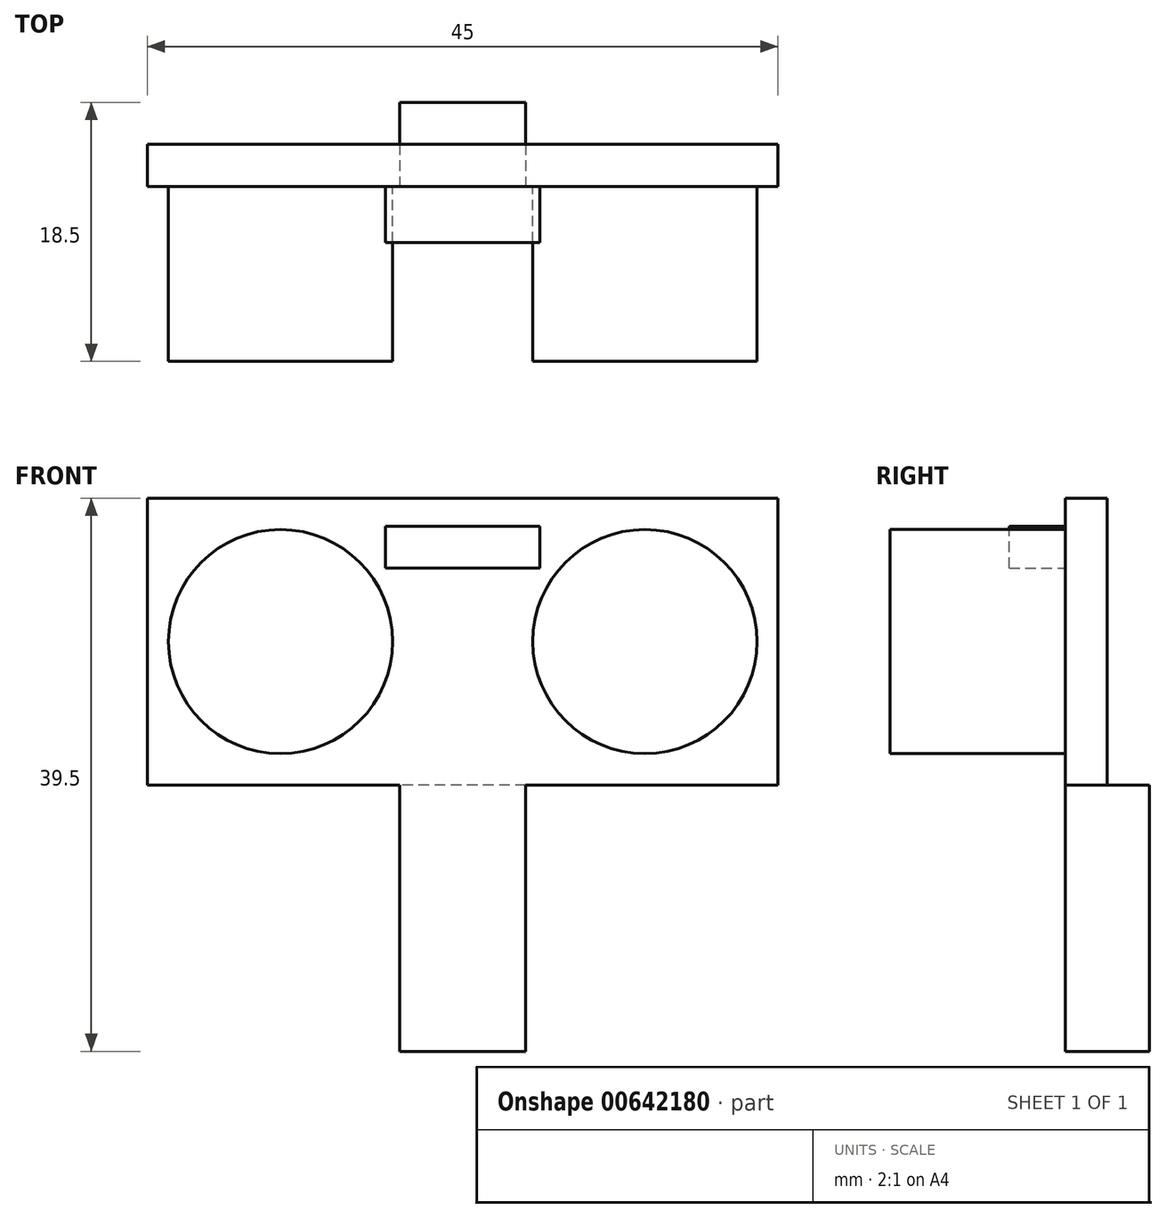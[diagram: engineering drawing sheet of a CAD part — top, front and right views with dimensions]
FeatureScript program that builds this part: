
annotation { "Feature Type Name" : "Feature", "Feature Type Description" : "" }
export const myFeature = defineFeature(function(context is Context, id is Id, definition is map)
    precondition{}
    {
        {
            var Q0;
            Q0=qCreatedBy(makeId("Front.planeOp"),FACE);
            var sketch = newSketch(context, id + "F0", { "sketchPlane" : qUnion([Q0])});
            skLineSegment(sketch, "E0.bottom", {"start": v(22.5, -10.25) * mm, "end": v(-22.5, -10.25) * mm});
            skLineSegment(sketch, "E0.top", {"start": v(22.5, 10.25) * mm, "end": v(-22.5, 10.25) * mm});
            skLineSegment(sketch, "E0.left", {"start": v(22.5, -10.25) * mm, "end": v(22.5, 10.25) * mm});
            skLineSegment(sketch, "E0.right", {"start": v(-22.5, -10.25) * mm, "end": v(-22.5, 10.25) * mm});
            skPoint(sketch, "E0.middle", {"position": v(0, 0) * mm});
            skSolve(sketch);
        }
        {
            var Q0;
            Q0 = qSketchRegion(id + "F0", true);
            extrude(context, id + "F1", {"entities" : qUnion([Q0]), "oppositeDirection" : true, "depth" : 3 * mm, "offsetDistance" : 25.4 * mm});
        }
        {
            var Q0;
            Q0=qCreatedBy(makeId("Front.planeOp"),FACE);
            var sketch = newSketch(context, id + "F2", { "sketchPlane" : qUnion([Q0])});
            skCircle(sketch, "E1", {"center": v(-13, 0) * mm, "radius": 8 * mm});
            skCircle(sketch, "E2", {"center": v(13, 0) * mm, "radius": 8 * mm});
            skLineSegment(sketch, "E3", {"start": v(13, 0) * mm, "end": v(0, 0) * mm, "construction": true});
            skLineSegment(sketch, "E4", {"start": v(0, 0) * mm, "end": v(-13, 0) * mm, "construction": true});
            skSolve(sketch);
        }
        {
            var Q0;
            Q0 = qSketchRegion(id + "F2", true);
            extrude(context, id + "F3", {"entities" : qUnion([Q0]), "operationType" : NewBodyOperationType.ADD, "depth" : 12.5 * mm, "offsetDistance" : 25.4 * mm});
        }
        {
            var Q0;
            Q0=qCreatedBy(makeId("Front.planeOp"),FACE);
            var sketch = newSketch(context, id + "F4", { "sketchPlane" : qUnion([Q0])});
            skLineSegment(sketch, "E5.bottom", {"start": v(-5.5, 5.25) * mm, "end": v(5.5, 5.25) * mm});
            skLineSegment(sketch, "E5.top", {"start": v(-5.5, 8.25) * mm, "end": v(5.5, 8.25) * mm});
            skLineSegment(sketch, "E5.left", {"start": v(-5.5, 5.25) * mm, "end": v(-5.5, 8.25) * mm});
            skLineSegment(sketch, "E5.right", {"start": v(5.5, 5.25) * mm, "end": v(5.5, 8.25) * mm});
            skSolve(sketch);
        }
        {
            var Q0;
            Q0 = qSketchRegion(id + "F4", true);
            extrude(context, id + "F5", {"entities" : qUnion([Q0]), "operationType" : NewBodyOperationType.ADD, "depth" : 4 * mm, "offsetDistance" : 25.4 * mm});
        }
        {
            var Q0;
            Q0=qCreatedBy(makeId("Front.planeOp"),FACE);
            var sketch = newSketch(context, id + "F6", { "sketchPlane" : qUnion([Q0])});
            skLineSegment(sketch, "E6", {"start": v(0, 0) * mm, "end": v(0, -39.5) * mm, "construction": true});
            skLineSegment(sketch, "E7.bottom", {"start": v(4.5, -10.25) * mm, "end": v(-4.5, -10.25) * mm});
            skLineSegment(sketch, "E7.top", {"start": v(4.5, -29.25) * mm, "end": v(-4.5, -29.25) * mm});
            skLineSegment(sketch, "E7.left", {"start": v(4.5, -10.25) * mm, "end": v(4.5, -29.25) * mm});
            skLineSegment(sketch, "E7.right", {"start": v(-4.5, -10.25) * mm, "end": v(-4.5, -29.25) * mm});
            skPoint(sketch, "E7.middle", {"position": v(0, -19.75) * mm});
            skSolve(sketch);
        }
        {
            var Q0;
            Q0 = qSketchRegion(id + "F6", true);
            extrude(context, id + "F7", {"entities" : qUnion([Q0]), "operationType" : NewBodyOperationType.ADD, "oppositeDirection" : true, "depth" : 6 * mm, "offsetDistance" : 25.4 * mm});
        }
    });
